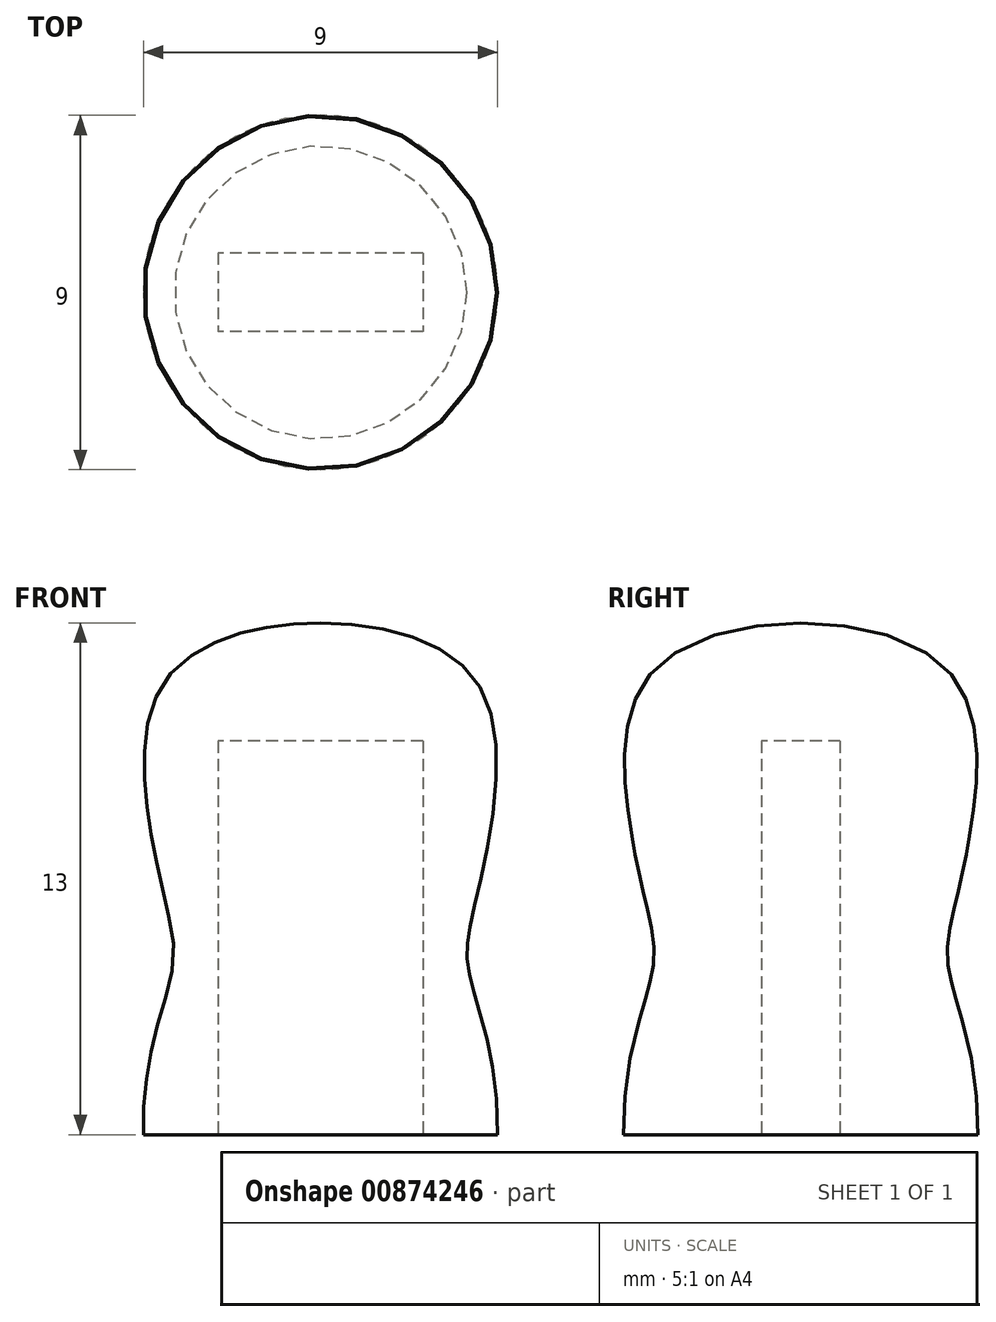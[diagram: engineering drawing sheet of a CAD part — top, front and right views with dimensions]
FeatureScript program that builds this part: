
annotation { "Feature Type Name" : "Feature", "Feature Type Description" : "" }
export const myFeature = defineFeature(function(context is Context, id is Id, definition is map)
    precondition{}
    {
        {
            var Q0;
            Q0=qCreatedBy(makeId("Front.planeOp"),FACE);
            var sketch = newSketch(context, id + "F0", { "sketchPlane" : qUnion([Q0])});
            skLineSegment(sketch, "E0", {"start": v(0, 0) * mm, "end": v(4.5, 0) * mm});
            skLineSegment(sketch, "E1", {"start": v(0, 0) * mm, "end": v(0, 13) * mm});
            skFitSpline(sketch, "E2", {"points": [v(0, 13) * mm, v(4.15, 11.18) * mm, v(3.88, 5.69) * mm, v(3.78, 4.09) * mm, v(4.5, 0) * mm], "startDerivative": vector(18.07, 0) * mm, "endDerivative": vector(-0.54, -21.95) * mm});
            skLineSegment(sketch, "E3", {"start": v(0, 13) * mm, "end": v(-11.87, 13) * mm, "construction": true});
            skSolve(sketch);
        }
        {
            var Q0;
            Q0=makeQuery(id+"F0.imprint","IMPRINT",FACE,{"disambiguationData":[TD([[makeQuery(id+"F0.imprint","IMPRINT",EDGE,{"derivedFrom":sQuery(id+"F0.wireOp",EDGE,"E0")}),1.0]])]});
            var Q1;
            Q1=sQuery(id+"F0.wireOp",EDGE,"E1");
            revolve(context, id + "F1", {"surfaceOperationType" : NewSurfaceOperationType.NEW, "entities" : qUnion([Q0]), "axis" : qUnion([Q1]), "revolveType" : RevolveType.FULL});
        }
        {
            var Q0;
            Q0=makeQuery(id+"F1.opRevolve","SWEPT_FACE",FACE,{"disambiguationData":[OSD([sQuery(id+"F0.wireOp",EDGE,"E0")])]});
            var sketch = newSketch(context, id + "F2", { "sketchPlane" : qUnion([Q0])});
            skLineSegment(sketch, "E4.bottom", {"start": v(2.6, -1) * mm, "end": v(-2.6, -1) * mm});
            skLineSegment(sketch, "E4.top", {"start": v(2.6, 1) * mm, "end": v(-2.6, 1) * mm});
            skLineSegment(sketch, "E4.left", {"start": v(2.6, -1) * mm, "end": v(2.6, 1) * mm});
            skLineSegment(sketch, "E4.right", {"start": v(-2.6, -1) * mm, "end": v(-2.6, 1) * mm});
            skPoint(sketch, "E4.middle", {"position": v(0, 0) * mm});
            skSolve(sketch);
        }
        {
            var Q0;
            Q0=makeQuery(id+"F2.imprint","IMPRINT",FACE,{"disambiguationData":[TD([[makeQuery(id+"F2.imprint","IMPRINT",EDGE,{"derivedFrom":sQuery(id+"F2.wireOp",EDGE,"E4.bottom")}),-1.0]])]});
            extrude(context, id + "F3", {"entities" : qUnion([Q0]), "operationType" : NewBodyOperationType.REMOVE, "oppositeDirection" : true, "depth" : 10 * mm, "offsetDistance" : 25 * mm});
        }
    });
